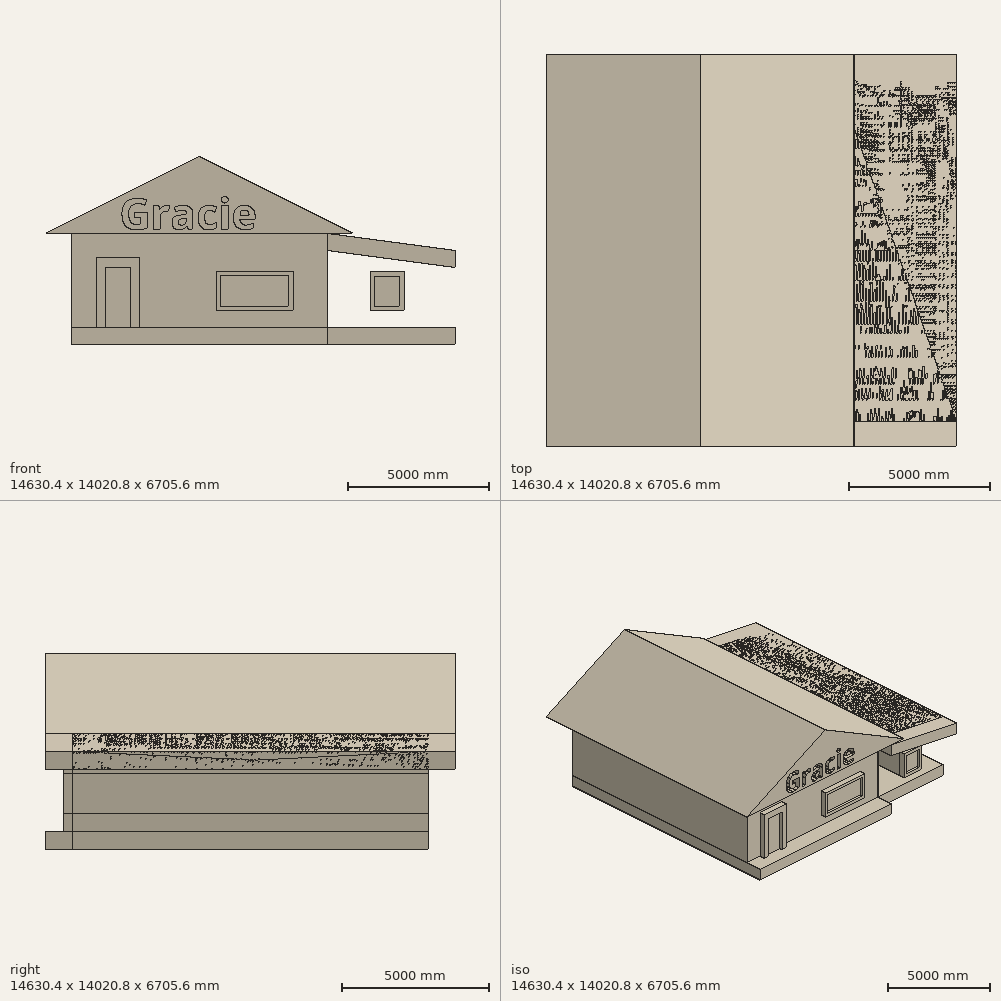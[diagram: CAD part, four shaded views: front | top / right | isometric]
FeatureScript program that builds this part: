
annotation { "Feature Type Name" : "Feature", "Feature Type Description" : "" }
export const myFeature = defineFeature(function(context is Context, id is Id, definition is map)
    precondition{}
    {
        {
            var Q0;
            Q0=qCreatedBy(makeId("Front.planeOp"),FACE);
            var sketch = newSketch(context, id + "F0", { "sketchPlane" : qUnion([Q0])});
            skLineSegment(sketch, "E0", {"start": v(0, 0) * mm, "end": v(-4572, 0) * mm});
            skLineSegment(sketch, "E1", {"start": v(0, 0) * mm, "end": v(4572, 0) * mm});
            skLineSegment(sketch, "E2", {"start": v(0, 0) * mm, "end": v(0, 2286) * mm, "construction": true});
            skLineSegment(sketch, "E3", {"start": v(0, 2286) * mm, "end": v(-4572, 0) * mm});
            skLineSegment(sketch, "E4", {"start": v(0, 2286) * mm, "end": v(4572, 0) * mm});
            skLineSegment(sketch, "E5", {"start": v(0, 2286) * mm, "end": v(0, 2743.2) * mm});
            skLineSegment(sketch, "E6", {"start": v(-4572, 0) * mm, "end": v(-5486.4, 0) * mm});
            skLineSegment(sketch, "E7", {"start": v(4572, 0) * mm, "end": v(5486.4, 0) * mm});
            skLineSegment(sketch, "E8", {"start": v(0, 2743.2) * mm, "end": v(-5486.4, 0) * mm});
            skLineSegment(sketch, "E9", {"start": v(0, 2743.2) * mm, "end": v(5486.4, 0) * mm});
            skLineSegment(sketch, "E10", {"start": v(-4572, 0) * mm, "end": v(-4572, -3352.8) * mm});
            skLineSegment(sketch, "E11", {"start": v(4572, 0) * mm, "end": v(4572, -3352.8) * mm});
            skLineSegment(sketch, "E12", {"start": v(-4572, -3352.8) * mm, "end": v(4572, -3352.8) * mm});
            skLineSegment(sketch, "E13", {"start": v(-4572, -3352.8) * mm, "end": v(-4572, -3962.4) * mm});
            skLineSegment(sketch, "E14", {"start": v(4572, -3352.8) * mm, "end": v(4572, -3962.4) * mm});
            skLineSegment(sketch, "E15", {"start": v(4572, -3962.4) * mm, "end": v(-4572, -3962.4) * mm});
            skLineSegment(sketch, "E16", {"start": v(4572, -3962.4) * mm, "end": v(9144, -3962.4) * mm});
            skLineSegment(sketch, "E17", {"start": v(4572, -3352.8) * mm, "end": v(9144, -3352.8) * mm});
            skLineSegment(sketch, "E18", {"start": v(9144, -3352.8) * mm, "end": v(9144, -3962.4) * mm});
            skLineSegment(sketch, "E19", {"start": v(9144, -3352.8) * mm, "end": v(9144, -609.6) * mm});
            skLineSegment(sketch, "E20", {"start": v(4572, 0) * mm, "end": v(9144, -609.6) * mm});
            skLineSegment(sketch, "E21", {"start": v(4572, -609.6) * mm, "end": v(9144, -1219.2) * mm});
            skLineSegment(sketch, "E22", {"start": v(4572, 0) * mm, "end": v(4572, -609.6) * mm});
            skLineSegment(sketch, "E23", {"start": v(-3352.8, -3352.8) * mm, "end": v(-3352.8, -1219.2) * mm});
            skLineSegment(sketch, "E24", {"start": v(-3657.6, -3352.8) * mm, "end": v(-3657.6, -860.76) * mm});
            skLineSegment(sketch, "E25", {"start": v(-2438.4, -1219.2) * mm, "end": v(-2438.4, -3352.8) * mm});
            skLineSegment(sketch, "E26", {"start": v(-3352.8, -1219.2) * mm, "end": v(-2438.4, -1219.2) * mm});
            skLineSegment(sketch, "E27", {"start": v(-2133.6, -3352.8) * mm, "end": v(-2133.6, -860.76) * mm});
            skLineSegment(sketch, "E28", {"start": v(-2133.6, -860.76) * mm, "end": v(-3657.6, -860.76) * mm});
            skLineSegment(sketch, "E29", {"start": v(0, 0) * mm, "end": v(0, -3962.4) * mm, "construction": true});
            skLineSegment(sketch, "E30.bottom", {"start": v(609.6, -1371.6) * mm, "end": v(3352.8, -1371.6) * mm});
            skLineSegment(sketch, "E30.top", {"start": v(609.6, -2743.2) * mm, "end": v(3352.8, -2743.2) * mm});
            skLineSegment(sketch, "E30.left", {"start": v(609.6, -1371.6) * mm, "end": v(609.6, -2743.2) * mm});
            skLineSegment(sketch, "E30.right", {"start": v(3352.8, -1371.6) * mm, "end": v(3352.8, -2743.2) * mm});
            skLineSegment(sketch, "E31.bottom", {"start": v(762, -1519.06) * mm, "end": v(3200.4, -1519.06) * mm});
            skLineSegment(sketch, "E31.top", {"start": v(762, -2590.8) * mm, "end": v(3200.4, -2590.8) * mm});
            skLineSegment(sketch, "E31.left", {"start": v(762, -1519.06) * mm, "end": v(762, -2590.8) * mm});
            skLineSegment(sketch, "E31.right", {"start": v(3200.4, -1519.06) * mm, "end": v(3200.4, -2590.8) * mm});
            skLineSegment(sketch, "E32.bottom", {"start": v(6096, -1373.04) * mm, "end": v(7315.2, -1373.04) * mm});
            skLineSegment(sketch, "E32.top", {"start": v(6096, -2744.64) * mm, "end": v(7315.2, -2744.64) * mm});
            skLineSegment(sketch, "E32.left", {"start": v(6096, -1373.04) * mm, "end": v(6096, -2744.64) * mm});
            skLineSegment(sketch, "E32.right", {"start": v(7315.2, -1373.04) * mm, "end": v(7315.2, -2744.64) * mm});
            skLineSegment(sketch, "E33.bottom", {"start": v(6248.4, -1542.76) * mm, "end": v(7162.8, -1542.76) * mm});
            skLineSegment(sketch, "E33.top", {"start": v(6248.4, -2592.24) * mm, "end": v(7162.8, -2592.24) * mm});
            skLineSegment(sketch, "E33.left", {"start": v(6248.4, -1542.76) * mm, "end": v(6248.4, -2592.24) * mm});
            skLineSegment(sketch, "E33.right", {"start": v(7162.8, -1542.76) * mm, "end": v(7162.8, -2592.24) * mm});
            skSolve(sketch);
        }
        {
            var Q0;
            Q0=makeQuery(id+"F0.imprint","IMPRINT",FACE,{"disambiguationData":[TD([[makeQuery(id+"F0.imprint","IMPRINT",EDGE,{"derivedFrom":sQuery(id+"F0.wireOp",EDGE,"E4")}),1.0]])]});
            var Q1;
            Q1=makeQuery(id+"F0.imprint","IMPRINT",FACE,{"disambiguationData":[TD([[makeQuery(id+"F0.imprint","IMPRINT",EDGE,{"derivedFrom":sQuery(id+"F0.wireOp",EDGE,"E3")}),-1.0]])]});
            extrude(context, id + "F1", {"entities" : qUnion([Q0, Q1]), "depth" : 914.4 * mm, "offsetDistance" : 30.48 * mm});
        }
        {
            var Q0;
            Q0=makeQuery(id+"F0.imprint","IMPRINT",FACE,{"disambiguationData":[TD([[makeQuery(id+"F0.imprint","IMPRINT",EDGE,{"derivedFrom":sQuery(id+"F0.wireOp",EDGE,"E3")}),-1.0]])]});
            var Q1;
            Q1=makeQuery(id+"F0.imprint","IMPRINT",FACE,{"disambiguationData":[TD([[makeQuery(id+"F0.imprint","IMPRINT",EDGE,{"derivedFrom":sQuery(id+"F0.wireOp",EDGE,"E4")}),1.0]])]});
            extrude(context, id + "F2", {"entities" : qUnion([Q0, Q1]), "operationType" : NewBodyOperationType.ADD, "oppositeDirection" : true, "depth" : 13106.4 * mm, "offsetDistance" : 30.48 * mm});
        }
        {
            var Q0;
            Q0=makeQuery(id+"F0.imprint","IMPRINT",FACE,{"disambiguationData":[TD([[makeQuery(id+"F0.imprint","IMPRINT",EDGE,{"derivedFrom":sQuery(id+"F0.wireOp",EDGE,"E0")}),-1.0]])]});
            extrude(context, id + "F3", {"entities" : qUnion([Q0]), "operationType" : NewBodyOperationType.ADD, "depth" : -12192 * mm, "offsetDistance" : 30.48 * mm});
        }
        {
            var Q0;
            {var subQ5=sQuery(id+"F0.wireOp",EDGE,"E13");Q0=makeQuery(id+"F0.imprint","IMPRINT",FACE,{"disambiguationData":[TD([[makeQuery(id+"F0.imprint","IMPRINT",EDGE,{"derivedFrom":subQ5}),1.0]])]});}
            var Q1;
            Q1=makeQuery(id+"F0.imprint","IMPRINT",FACE,{"disambiguationData":[TD([[makeQuery(id+"F0.imprint","IMPRINT",EDGE,{"derivedFrom":sQuery(id+"F0.wireOp",EDGE,"E0")}),-1.0]])]});
            extrude(context, id + "F4", {"entities" : qUnion([Q0, Q1]), "operationType" : NewBodyOperationType.ADD, "depth" : 914.4 * mm, "offsetDistance" : 30.48 * mm});
        }
        {
            var Q0;
            {var subQ5=sQuery(id+"F0.wireOp",EDGE,"E13");Q0=makeQuery(id+"F0.imprint","IMPRINT",FACE,{"disambiguationData":[TD([[makeQuery(id+"F0.imprint","IMPRINT",EDGE,{"derivedFrom":subQ5}),1.0]])]});}
            extrude(context, id + "F5", {"entities" : qUnion([Q0]), "operationType" : NewBodyOperationType.ADD, "depth" : -12192 * mm, "offsetDistance" : 30.48 * mm});
        }
        {
            var Q0;
            Q0=makeQuery(id+"F0.imprint","IMPRINT",FACE,{"disambiguationData":[TD([[makeQuery(id+"F0.imprint","IMPRINT",EDGE,{"derivedFrom":sQuery(id+"F0.wireOp",EDGE,"E0")}),1.0]])]});
            var Q1;
            Q1=makeQuery(id+"F0.imprint","IMPRINT",FACE,{"disambiguationData":[TD([[makeQuery(id+"F0.imprint","IMPRINT",EDGE,{"derivedFrom":sQuery(id+"F0.wireOp",EDGE,"E11")}),1.0]])]});
            var Q2;
            Q2=makeQuery(id+"F0.imprint","IMPRINT",FACE,{"disambiguationData":[TD([[makeQuery(id+"F0.imprint","IMPRINT",EDGE,{"derivedFrom":sQuery(id+"F0.wireOp",EDGE,"E31.bottom")}),-1.0]])]});
            var Q3;
            {var subQ0=sQuery(id+"F0.wireOp",EDGE,"E23");Q3=makeQuery(id+"F0.imprint","IMPRINT",FACE,{"disambiguationData":[TD([[makeQuery(id+"F0.imprint","IMPRINT",EDGE,{"derivedFrom":subQ0}),-1.0]])]});}
            var Q4;
            {var subQ4=sQuery(id+"F0.wireOp",EDGE,"E23");Q4=makeQuery(id+"F0.imprint","IMPRINT",FACE,{"disambiguationData":[TD([[makeQuery(id+"F0.imprint","IMPRINT",EDGE,{"derivedFrom":subQ4}),1.0]])]});}
            var Q5;
            Q5=makeQuery(id+"F0.imprint","IMPRINT",FACE,{"disambiguationData":[TD([[makeQuery(id+"F0.imprint","IMPRINT",EDGE,{"derivedFrom":sQuery(id+"F0.wireOp",EDGE,"E33.bottom")}),-1.0]])]});
            var Q6;
            Q6=makeQuery(id+"F0.imprint","IMPRINT",FACE,{"disambiguationData":[TD([[makeQuery(id+"F0.imprint","IMPRINT",EDGE,{"derivedFrom":sQuery(id+"F0.wireOp",EDGE,"E30.bottom")}),-1.0]])]});
            var Q7;
            Q7=makeQuery(id+"F0.imprint","IMPRINT",FACE,{"disambiguationData":[TD([[makeQuery(id+"F0.imprint","IMPRINT",EDGE,{"derivedFrom":sQuery(id+"F0.wireOp",EDGE,"E32.bottom")}),-1.0]])]});
            extrude(context, id + "F6", {"entities" : qUnion([Q0, Q1, Q2, Q3, Q4, Q5, Q6, Q7]), "depth" : -12192 * mm, "offsetDistance" : 30.48 * mm});
        }
        {
            var Q0;
            {var subQ4=sQuery(id+"F0.wireOp",EDGE,"E23");Q0=makeQuery(id+"F0.imprint","IMPRINT",FACE,{"disambiguationData":[TD([[makeQuery(id+"F0.imprint","IMPRINT",EDGE,{"derivedFrom":subQ4}),1.0]])]});}
            var Q1;
            Q1=makeQuery(id+"F0.imprint","IMPRINT",FACE,{"disambiguationData":[TD([[makeQuery(id+"F0.imprint","IMPRINT",EDGE,{"derivedFrom":sQuery(id+"F0.wireOp",EDGE,"E30.bottom")}),-1.0]])]});
            var Q2;
            Q2=makeQuery(id+"F0.imprint","IMPRINT",FACE,{"disambiguationData":[TD([[makeQuery(id+"F0.imprint","IMPRINT",EDGE,{"derivedFrom":sQuery(id+"F0.wireOp",EDGE,"E32.bottom")}),-1.0]])]});
            extrude(context, id + "F7", {"entities" : qUnion([Q0, Q1, Q2]), "depth" : 304.8 * mm, "offsetDistance" : 30.48 * mm});
        }
        {
            var Q0;
            {var subQ0=sQuery(id+"F0.wireOp",EDGE,"E23");Q0=makeQuery(id+"F0.imprint","IMPRINT",FACE,{"disambiguationData":[TD([[makeQuery(id+"F0.imprint","IMPRINT",EDGE,{"derivedFrom":subQ0}),-1.0]])]});}
            var Q1;
            Q1=makeQuery(id+"F0.imprint","IMPRINT",FACE,{"disambiguationData":[TD([[makeQuery(id+"F0.imprint","IMPRINT",EDGE,{"derivedFrom":sQuery(id+"F0.wireOp",EDGE,"E31.bottom")}),-1.0]])]});
            var Q2;
            Q2=makeQuery(id+"F0.imprint","IMPRINT",FACE,{"disambiguationData":[TD([[makeQuery(id+"F0.imprint","IMPRINT",EDGE,{"derivedFrom":sQuery(id+"F0.wireOp",EDGE,"E33.bottom")}),-1.0]])]});
            extrude(context, id + "F8", {"entities" : qUnion([Q0, Q1, Q2]), "depth" : 152.4 * mm, "offsetDistance" : 30.48 * mm});
        }
        {
            var Q0;
            Q0=makeQuery(id+"F0.imprint","IMPRINT",FACE,{"disambiguationData":[TD([[makeQuery(id+"F0.imprint","IMPRINT",EDGE,{"derivedFrom":sQuery(id+"F0.wireOp",EDGE,"E14")}),1.0]])]});
            extrude(context, id + "F9", {"entities" : qUnion([Q0]), "depth" : -12192 * mm, "offsetDistance" : 30.48 * mm});
        }
        {
            var Q0;
            {var subQ0=sQuery(id+"F0.wireOp",EDGE,"E20");Q0=makeQuery(id+"F0.imprint","IMPRINT",FACE,{"disambiguationData":[TD([[makeQuery(id+"F0.imprint","IMPRINT",EDGE,{"derivedFrom":subQ0}),-1.0]])]});}
            extrude(context, id + "F10", {"entities" : qUnion([Q0]), "depth" : 914.4 * mm, "offsetDistance" : 30.48 * mm});
        }
        {
            var Q0;
            {var subQ0=sQuery(id+"F0.wireOp",EDGE,"E20");Q0=makeQuery(id+"F0.imprint","IMPRINT",FACE,{"disambiguationData":[TD([[makeQuery(id+"F0.imprint","IMPRINT",EDGE,{"derivedFrom":subQ0}),-1.0]])]});}
            extrude(context, id + "F11", {"entities" : qUnion([Q0]), "depth" : -13106.4 * mm, "offsetDistance" : 30.48 * mm});
        }
        {
            var Q0;
            Q0=qCreatedBy(makeId("Front.planeOp"),FACE);
            var sketch = newSketch(context, id + "F12", { "sketchPlane" : qUnion([Q0])});
            skText(sketch, "E34", { "text": "Gracie", "fontName": "OpenSans-Bold.ttf"});
            const initialGuessF12  = {"E34": [-2.84829, 0.14137, 1, 0, 1.1067]};
            skSetInitialGuess(sketch, initialGuessF12);
            skSolve(sketch);
        }
        {
            var Q0;
            Q0=makeQuery(id+"F12.imprint","IMPRINT",FACE,{"disambiguationData":[TD([[makeQuery(id+"F12.imprint","IMPRINT",EDGE,{"derivedFrom":sQuery(id+"F12.wireOp",EDGE,"E34.sketch_text.stroke-0")}),-1.0]])]});
            var Q1;
            Q1=makeQuery(id+"F12.imprint","IMPRINT",FACE,{"disambiguationData":[TD([[makeQuery(id+"F12.imprint","IMPRINT",EDGE,{"derivedFrom":sQuery(id+"F12.wireOp",EDGE,"E34.sketch_text.stroke-19")}),-1.0]])]});
            var Q2;
            Q2=makeQuery(id+"F12.imprint","IMPRINT",FACE,{"disambiguationData":[TD([[makeQuery(id+"F12.imprint","IMPRINT",EDGE,{"derivedFrom":sQuery(id+"F12.wireOp",EDGE,"E34.sketch_text.stroke-57")}),-1.0]])]});
            var Q3;
            Q3=makeQuery(id+"F12.imprint","IMPRINT",FACE,{"disambiguationData":[TD([[makeQuery(id+"F12.imprint","IMPRINT",EDGE,{"derivedFrom":sQuery(id+"F12.wireOp",EDGE,"E34.sketch_text.stroke-71")}),-1.0]])]});
            var Q4;
            Q4=makeQuery(id+"F12.imprint","IMPRINT",FACE,{"disambiguationData":[TD([[makeQuery(id+"F12.imprint","IMPRINT",EDGE,{"derivedFrom":sQuery(id+"F12.wireOp",EDGE,"E34.sketch_text.stroke-76")}),-1.0]])]});
            var Q5;
            Q5=makeQuery(id+"F12.imprint","IMPRINT",FACE,{"disambiguationData":[TD([[makeQuery(id+"F12.imprint","IMPRINT",EDGE,{"derivedFrom":sQuery(id+"F12.wireOp",EDGE,"E34.sketch_text.stroke-32")}),-1.0]])]});
            var Q6;
            Q6=makeQuery(id+"F12.imprint","IMPRINT",FACE,{"disambiguationData":[TD([[makeQuery(id+"F12.imprint","IMPRINT",EDGE,{"derivedFrom":sQuery(id+"F12.wireOp",EDGE,"E34.sketch_text.stroke-80")}),-1.0]])]});
            extrude(context, id + "F13", {"entities" : qUnion([Q0, Q1, Q2, Q3, Q4, Q5, Q6]), "operationType" : NewBodyOperationType.REMOVE, "depth" : 1524 * mm, "offsetDistance" : 30.48 * mm});
        }
    });
